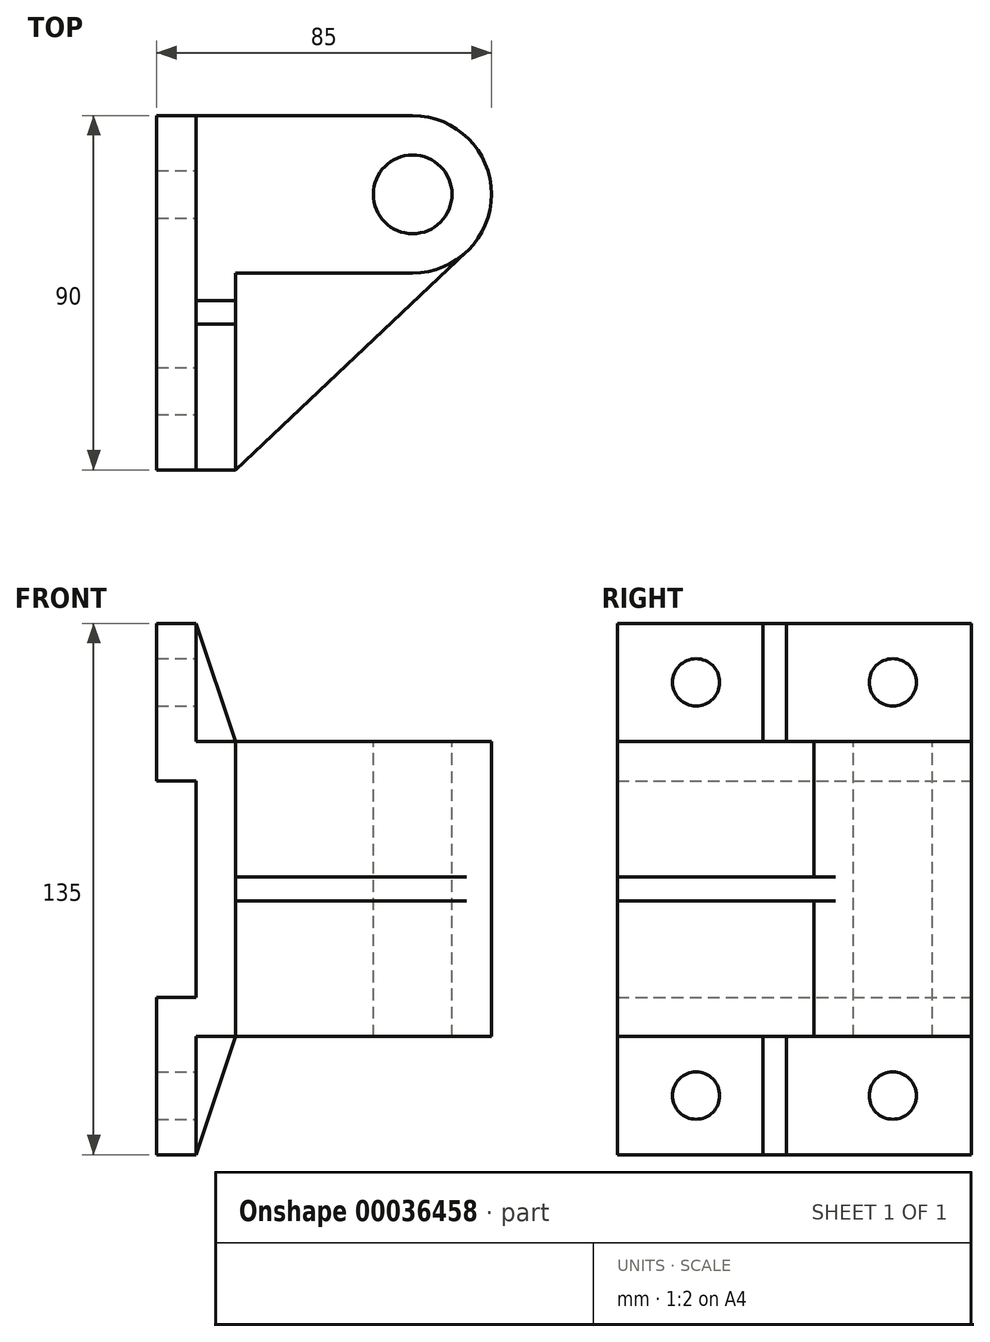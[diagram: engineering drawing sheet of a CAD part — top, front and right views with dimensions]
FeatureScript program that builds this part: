
annotation { "Feature Type Name" : "Feature", "Feature Type Description" : "" }
export const myFeature = defineFeature(function(context is Context, id is Id, definition is map)
    precondition{}
    {
        {
            var Q0;
            Q0=qCreatedBy(makeId("Front.planeOp"),FACE);
            var sketch = newSketch(context, id + "F0", { "sketchPlane" : qUnion([Q0])});
            skLineSegment(sketch, "E0", {"start": v(-20, 67.5) * mm, "end": v(-20, 27.5) * mm});
            skLineSegment(sketch, "E1", {"start": v(-20, 27.5) * mm, "end": v(-10, 27.5) * mm});
            skLineSegment(sketch, "E2", {"start": v(-10, 27.5) * mm, "end": v(-10, -27.5) * mm});
            skLineSegment(sketch, "E3", {"start": v(-10, -27.5) * mm, "end": v(-20, -27.5) * mm});
            skLineSegment(sketch, "E4", {"start": v(-20, -27.5) * mm, "end": v(-20, -67.5) * mm});
            skLineSegment(sketch, "E5.0", {"start": v(-10, -37.5) * mm, "end": v(-10, -67.5) * mm});
            skLineSegment(sketch, "E5.1", {"start": v(0, -37.5) * mm, "end": v(-10, -37.5) * mm});
            skLineSegment(sketch, "E5.2", {"start": v(0, 37.5) * mm, "end": v(0, -37.5) * mm});
            skLineSegment(sketch, "E5.3", {"start": v(-10, 37.5) * mm, "end": v(0, 37.5) * mm});
            skLineSegment(sketch, "E5.4", {"start": v(-10, 67.5) * mm, "end": v(-10, 37.5) * mm});
            skLineSegment(sketch, "E6", {"start": v(-20, 67.5) * mm, "end": v(-10, 67.5) * mm});
            skLineSegment(sketch, "E7", {"start": v(-20, -67.5) * mm, "end": v(-10, -67.5) * mm});
            skSolve(sketch);
        }
        {
            var Q0;
            Q0=makeQuery(id+"F0.imprint","IMPRINT",FACE,{"disambiguationData":[TD([[makeQuery(id+"F0.imprint","IMPRINT",EDGE,{"derivedFrom":sQuery(id+"F0.wireOp",EDGE,"E0")}),1.0]])]});
            extrude(context, id + "F1", {"entities" : qUnion([Q0]), "endBound" : BoundingType.SYMMETRIC, "depth" : 90 * mm});
        }
        {
            var Q0;
            Q0=makeQuery(id+"F1.opExtrude","SWEPT_FACE",FACE,{"disambiguationData":[OSD([sQuery(id+"F0.wireOp",EDGE,"E5.3")])]});
            var sketch = newSketch(context, id + "F2", { "sketchPlane" : qUnion([Q0])});
            skArc(sketch, "E8", {"start": v(45, 5) * mm, "mid": v(65, 25) * mm, "end": v(45, 45) * mm});
            skLineSegment(sketch, "E9", {"start": v(0, 45) * mm, "end": v(45, 45) * mm});
            skLineSegment(sketch, "E10", {"start": v(45, 5) * mm, "end": v(0, 5) * mm});
            skCircle(sketch, "E11", {"center": v(45, 25) * mm, "radius": 10 * mm});
            skSolve(sketch);
        }
        {
            var Q0;
            Q0=makeQuery(id+"F2.imprint","IMPRINT",FACE,{"disambiguationData":[TD([[makeQuery(id+"F2.imprint","IMPRINT",EDGE,{"derivedFrom":sQuery(id+"F2.wireOp",EDGE,"E8")}),1.0]])]});
            var Q1;
            Q1=makeQuery(id+"F1.opExtrude","SWEPT_FACE",FACE,{"disambiguationData":[OSD([sQuery(id+"F0.wireOp",EDGE,"E5.1")])]});
            extrude(context, id + "F3", {"entities" : qUnion([Q0]), "operationType" : NewBodyOperationType.ADD, "endBound" : BoundingType.UP_TO_SURFACE, "oppositeDirection" : true, "endBoundEntityFace" : qUnion([Q1]), "depth" : 25 * mm});
        }
        {
            var Q0;
            Q0=qCreatedBy(makeId("Top.planeOp"),FACE);
            var sketch = newSketch(context, id + "F4", { "sketchPlane" : qUnion([Q0])});
            skLineSegment(sketch, "E12", {"start": v(0, -45) * mm, "end": v(58.73, 10.46) * mm});
            skLineSegment(sketch, "E13.0", {"start": v(0, -45) * mm, "end": v(0, 5) * mm});
            skLineSegment(sketch, "E14.0", {"start": v(45, 5) * mm, "end": v(0, 5) * mm});
            skArc(sketch, "E15.0", {"start": v(45, 5) * mm, "mid": v(52.39, 6.41) * mm, "end": v(58.73, 10.46) * mm});
            skPoint(sketch, "E16.orphan", {"position": v(45, 45) * mm});
            skSolve(sketch);
        }
        {
            var Q0;
            Q0=makeQuery(id+"F4.imprint","IMPRINT",FACE,{"disambiguationData":[TD([[makeQuery(id+"F4.imprint","IMPRINT",EDGE,{"derivedFrom":sQuery(id+"F4.wireOp",EDGE,"E12")}),1.0]])]});
            extrude(context, id + "F5", {"entities" : qUnion([Q0]), "operationType" : NewBodyOperationType.ADD, "endBound" : BoundingType.SYMMETRIC, "depth" : 6 * mm});
        }
        {
            var Q0;
            Q0=makeQuery(id+"F1.opExtrude","CAP_FACE",FACE,{"disambiguationData":[OSD([sQuery(id+"F0.wireOp",EDGE,"E0"),sQuery(id+"F0.wireOp",EDGE,"E1"),sQuery(id+"F0.wireOp",EDGE,"E2"),sQuery(id+"F0.wireOp",EDGE,"E3"),sQuery(id+"F0.wireOp",EDGE,"E4"),sQuery(id+"F0.wireOp",EDGE,"E5.0"),sQuery(id+"F0.wireOp",EDGE,"E5.1"),sQuery(id+"F0.wireOp",EDGE,"E5.2"),sQuery(id+"F0.wireOp",EDGE,"E5.3"),sQuery(id+"F0.wireOp",EDGE,"E5.4"),sQuery(id+"F0.wireOp",EDGE,"E6"),sQuery(id+"F0.wireOp",EDGE,"E7")])],"isStart":false});
            cPlane(context, id + "F6", {"entities" : qUnion([Q0]), "cplaneType" : CPlaneType.OFFSET, "offset" : 37 * mm, "oppositeDirection" : true, "width" : 150 * mm, "height" : 150 * mm});
        }
        {
            var Q0;
            Q0=qCreatedBy(id+"F6.planeOp",FACE);
            var sketch = newSketch(context, id + "F7", { "sketchPlane" : qUnion([Q0])});
            skLineSegment(sketch, "E17", {"start": v(-10, 67.5) * mm, "end": v(0, 37.5) * mm});
            skLineSegment(sketch, "E18.0", {"start": v(-10, 67.5) * mm, "end": v(-10, 37.5) * mm});
            skLineSegment(sketch, "E19.0", {"start": v(-10, 37.5) * mm, "end": v(0, 37.5) * mm});
            skSolve(sketch);
        }
        {
            var Q0;
            Q0=makeQuery(id+"F7.imprint","IMPRINT",FACE,{"disambiguationData":[TD([[makeQuery(id+"F7.imprint","IMPRINT",EDGE,{"derivedFrom":sQuery(id+"F7.wireOp",EDGE,"E17")}),-1.0]])]});
            extrude(context, id + "F8", {"entities" : qUnion([Q0]), "operationType" : NewBodyOperationType.ADD, "oppositeDirection" : true, "depth" : 6 * mm});
        }
        {
            var Q0;
            Q0=makeQuery(id+"F1.opExtrude","SWEPT_BODY",BODY,{"disambiguationData":[OSD([sQuery(id+"F0.wireOp",EDGE,"E0"),sQuery(id+"F0.wireOp",EDGE,"E1"),sQuery(id+"F0.wireOp",EDGE,"E2"),sQuery(id+"F0.wireOp",EDGE,"E3"),sQuery(id+"F0.wireOp",EDGE,"E4"),sQuery(id+"F0.wireOp",EDGE,"E5.0"),sQuery(id+"F0.wireOp",EDGE,"E5.1"),sQuery(id+"F0.wireOp",EDGE,"E5.2"),sQuery(id+"F0.wireOp",EDGE,"E5.3"),sQuery(id+"F0.wireOp",EDGE,"E5.4"),sQuery(id+"F0.wireOp",EDGE,"E6"),sQuery(id+"F0.wireOp",EDGE,"E7")])]});
            var Q1;
            Q1=qCreatedBy(makeId("Top.planeOp"),FACE);
            mirror(context, id + "F9", {"operationType" : NewBodyOperationType.ADD, "entities" : qUnion([Q0]), "mirrorPlane" : qUnion([Q1])});
        }
        {
            var Q0;
            {var subQ0=sQuery(id+"F0.wireOp",EDGE,"E5.4");var subQ1=sQuery(id+"F7.wireOp",EDGE,"E17");Q0=makeQuery(id+"F8.boolean.opBoolean","SPLIT",FACE,{"disambiguationData":[TD([makeQuery(id+"F8.opExtrude","CAP_FACE",FACE,{"disambiguationData":[OSD([subQ1,sQuery(id+"F7.wireOp",EDGE,"E18.0"),sQuery(id+"F7.wireOp",EDGE,"E19.0")])],"isStart":true})])],"derivedFrom":makeQuery(id+"F1.opExtrude","SWEPT_FACE",FACE,{"disambiguationData":[OSD([subQ0])]})});}
            var sketch = newSketch(context, id + "F10", { "sketchPlane" : qUnion([Q0])});
            skCircle(sketch, "E20", {"center": v(-25, 52.5) * mm, "radius": 6 * mm});
            skCircle(sketch, "E21.1.0.0", {"center": v(25, 52.5) * mm, "radius": 6 * mm});
            skLineSegment(sketch, "E21.direction1", {"start": v(-25, 52.5) * mm, "end": v(25, 52.5) * mm, "construction": true});
            skCircle(sketch, "E22.1.0.0", {"center": v(-25, -52.5) * mm, "radius": 6 * mm});
            skCircle(sketch, "E22.1.0.1", {"center": v(25, -52.5) * mm, "radius": 6 * mm});
            skLineSegment(sketch, "E22.direction1", {"start": v(-25, 52.5) * mm, "end": v(-25, -52.5) * mm, "construction": true});
            skSolve(sketch);
        }
        {
            var Q0;
            Q0 = qSketchRegion(id + "F10", true);
            extrude(context, id + "F11", {"entities" : qUnion([Q0]), "operationType" : NewBodyOperationType.REMOVE, "endBound" : BoundingType.THROUGH_ALL, "oppositeDirection" : true, "depth" : 25 * mm});
        }
    });
